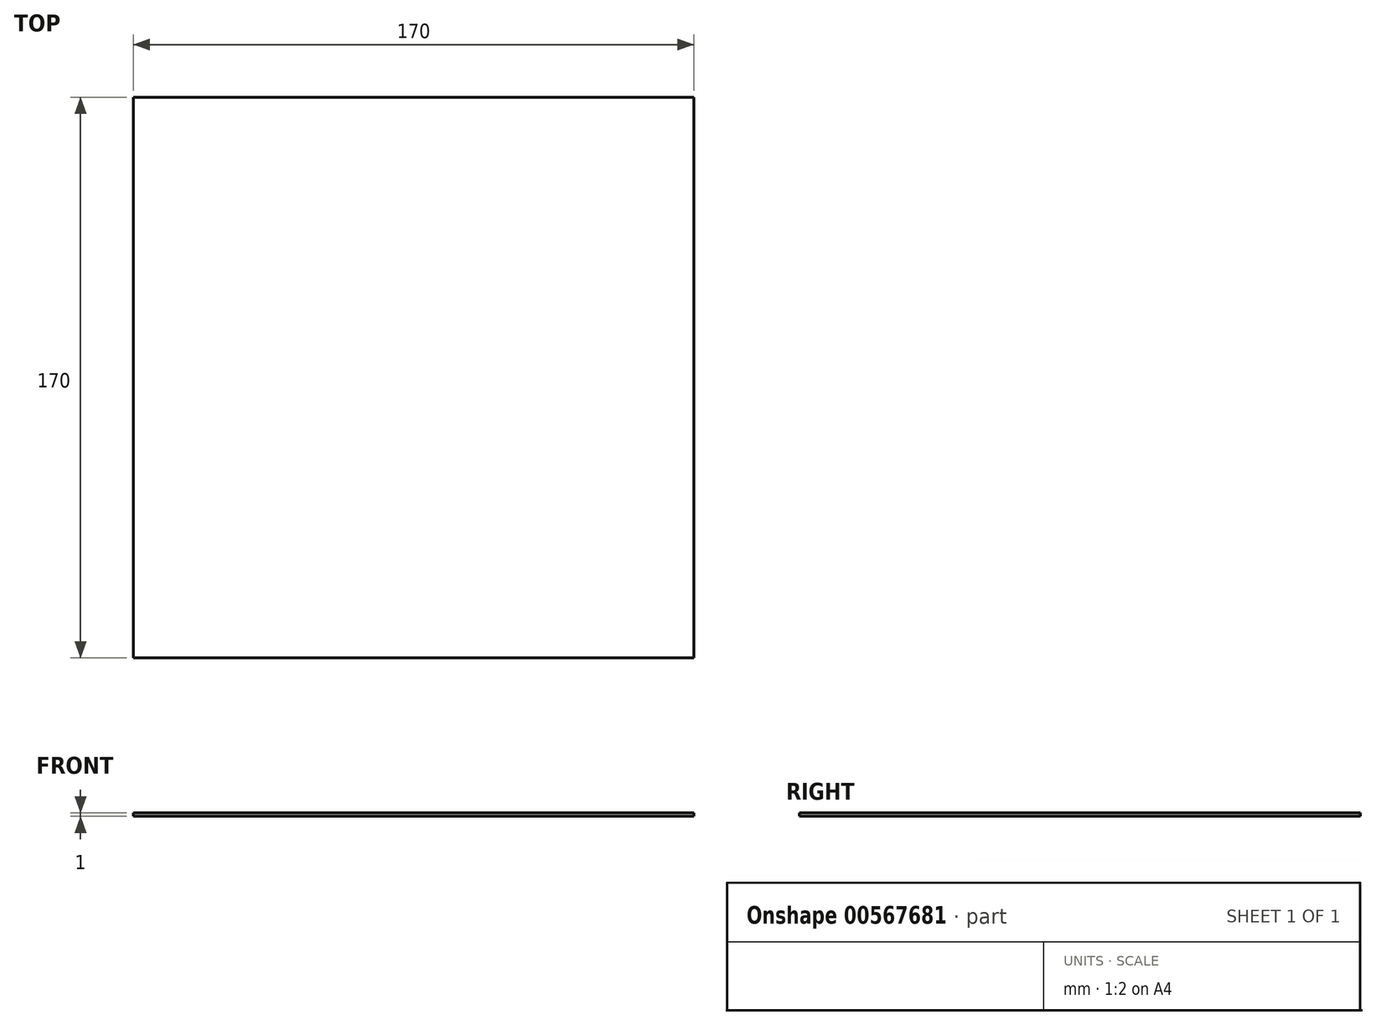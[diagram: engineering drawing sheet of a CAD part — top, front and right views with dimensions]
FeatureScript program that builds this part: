
annotation { "Feature Type Name" : "Feature", "Feature Type Description" : "" }
export const myFeature = defineFeature(function(context is Context, id is Id, definition is map)
    precondition{}
    {
        {
            var Q0;
            Q0=qCreatedBy(makeId("Top.planeOp"),FACE);
            var sketch = newSketch(context, id + "F0", { "sketchPlane" : qUnion([Q0])});
            skLineSegment(sketch, "E0.bottom", {"start": v(85, 85) * mm, "end": v(-85, 85) * mm});
            skLineSegment(sketch, "E0.top", {"start": v(85, -85) * mm, "end": v(-85, -85) * mm});
            skLineSegment(sketch, "E0.left", {"start": v(85, 85) * mm, "end": v(85, -85) * mm});
            skLineSegment(sketch, "E0.right", {"start": v(-85, 85) * mm, "end": v(-85, -85) * mm});
            skPoint(sketch, "E0.middle", {"position": v(0, 0) * mm});
            skSolve(sketch);
        }
        {
            var Q0;
            Q0=makeQuery(id+"F0.imprint","IMPRINT",FACE,{"disambiguationData":[TD([[makeQuery(id+"F0.imprint","IMPRINT",EDGE,{"derivedFrom":sQuery(id+"F0.wireOp",EDGE,"E0.bottom")}),1.0]])]});
            extrude(context, id + "F1", {"entities" : qUnion([Q0]), "depth" : 1 * mm, "offsetDistance" : 25 * mm});
        }
    });
